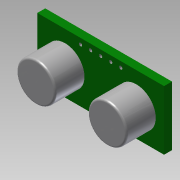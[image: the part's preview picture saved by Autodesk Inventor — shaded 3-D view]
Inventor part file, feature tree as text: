
AUTODESK INVENTOR PART (.ipt)
format: ipt  version: 2015 SP1 (Build 190203100, 203)  size: 138,240 bytes
history: native  units: mm
features: extrude x3, sketch x2, fillet x1, projected_geometry x1
ambient origin geometry x8: Origin, YZ Plane, XZ Plane, XY Plane, X Axis, Y Axis, Z Axis, Center Point
bodies: Solid1 (feature_tree)
feature tree (7):
  extrude  "Extrusion1"  Depth=15.0mm
  sketch  "Sketch2"  dims[d4=2.0mm d5=0.0mm d8=9.8mm d11=32.0mm d12=15.0mm d16=8.0mm d17=9.8mm d19=9.0mm d20=9.0mm d21=7.4mm d22=0.0mm d23=0.5mm d24=0.8mm d25=1.44mm d26=0.8mm d27=2.54mm d28=0.8mm d29=2.54mm d30=7.4mm d31=0.0mm]
  extrude  "Extrusion3"  Depth=7.4mm
  fillet  "Fillet2"  Radius=32.0mm
  extrude  "Extrusion4"  Depth=15.0mm
  sketch  "Sketch1"  dims[d0=32.0mm d1=15.0mm]
  projected_geometry  "Projected Loop1"
